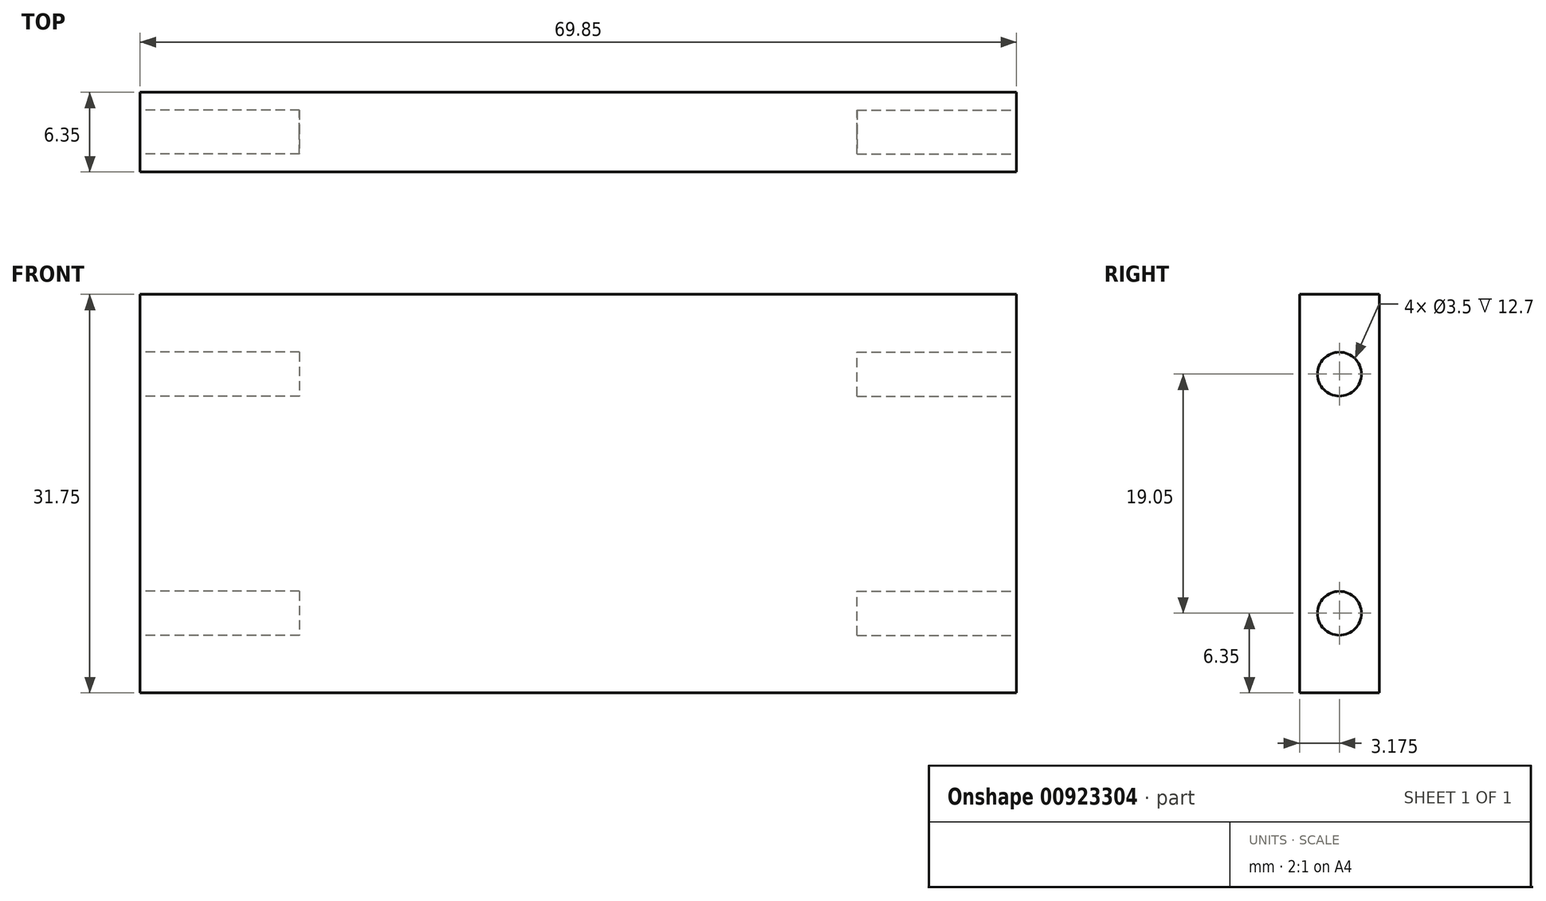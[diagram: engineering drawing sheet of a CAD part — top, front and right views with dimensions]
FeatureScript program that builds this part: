
annotation { "Feature Type Name" : "Feature", "Feature Type Description" : "" }
export const myFeature = defineFeature(function(context is Context, id is Id, definition is map)
    precondition{}
    {
        {
            var Q0;
            Q0=qCreatedBy(makeId("Top.planeOp"),FACE);
            var sketch = newSketch(context, id + "F0", { "sketchPlane" : qUnion([Q0])});
            skLineSegment(sketch, "E0.bottom", {"start": v(0, 0) * mm, "end": v(69.85, 0) * mm});
            skLineSegment(sketch, "E0.top", {"start": v(0, -6.35) * mm, "end": v(69.85, -6.35) * mm});
            skLineSegment(sketch, "E0.left", {"start": v(0, 0) * mm, "end": v(0, -6.35) * mm});
            skLineSegment(sketch, "E0.right", {"start": v(69.85, 0) * mm, "end": v(69.85, -6.35) * mm});
            skSolve(sketch);
        }
        {
            var Q0;
            Q0 = qSketchRegion(id + "F0", true);
            extrude(context, id + "F1", {"entities" : qUnion([Q0]), "depth" : 31.75 * mm, "offsetDistance" : 25.4 * mm});
        }
        {
            var Q0;
            Q0=makeQuery(id+"F1.opExtrude","SWEPT_FACE",FACE,{"disambiguationData":[OSD([sQuery(id+"F0.wireOp",EDGE,"E0.right")])]});
            var sketch = newSketch(context, id + "F2", { "sketchPlane" : qUnion([Q0])});
            skLineSegment(sketch, "E1", {"start": v(-3.17, 31.75) * mm, "end": v(-3.17, 0) * mm, "construction": true});
            skCircle(sketch, "E2", {"center": v(-3.17, 25.4) * mm, "radius": 1.75 * mm});
            skCircle(sketch, "E3", {"center": v(-3.17, 6.35) * mm, "radius": 1.75 * mm});
            skSolve(sketch);
        }
        {
            var Q0;
            Q0 = qSketchRegion(id + "F2", true);
            extrude(context, id + "F3", {"entities" : qUnion([Q0]), "operationType" : NewBodyOperationType.REMOVE, "oppositeDirection" : true, "depth" : 12.7 * mm, "offsetDistance" : 25.4 * mm});
        }
        {
            var Q0;
            Q0=makeQuery(id+"F1.opExtrude","SWEPT_FACE",FACE,{"disambiguationData":[OSD([sQuery(id+"F0.wireOp",EDGE,"E0.left")])]});
            var sketch = newSketch(context, id + "F4", { "sketchPlane" : qUnion([Q0])});
            skLineSegment(sketch, "E4", {"start": v(3.17, 0) * mm, "end": v(3.17, 31.75) * mm, "construction": true});
            skCircle(sketch, "E5", {"center": v(3.18, 6.35) * mm, "radius": 1.75 * mm});
            skCircle(sketch, "E6", {"center": v(3.17, 25.4) * mm, "radius": 1.75 * mm});
            skSolve(sketch);
        }
        {
            var Q0;
            Q0 = qSketchRegion(id + "F4", true);
            extrude(context, id + "F5", {"entities" : qUnion([Q0]), "operationType" : NewBodyOperationType.REMOVE, "oppositeDirection" : true, "depth" : 12.7 * mm, "offsetDistance" : 25.4 * mm});
        }
    });
